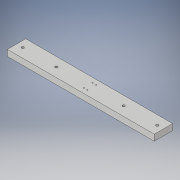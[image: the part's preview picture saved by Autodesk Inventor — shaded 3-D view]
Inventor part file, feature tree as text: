
AUTODESK INVENTOR PART (.ipt)
format: ipt  version: 2018 (Build 220112000, 112)  size: 114,688 bytes
history: native  units: in
note: dims shown in document units (in); Inventor stores cm internally (conversion verified against a paired STEP export)
features: sketch x3, hole x2, extrude x1
ambient origin geometry x8: Origin, YZ Plane, XZ Plane, XY Plane, X Axis, Y Axis, Z Axis, Center Point
bodies: Solid1 (feature_tree)
feature tree (6):
  extrude  "Extrusion1"  Depth=3.0in
  hole  "Hole1"  [1 undecoded]
  hole  "Hole2"  [1 undecoded]
  sketch  "Sketch1"  dims[d0=24.0in d1=3.0in]
  sketch  "Sketch2"  dims[d2=1.0in d3=0.0in d4=11.0in]
  sketch  "Sketch3"  dims[d5=5.5in d6=0.397in d7=0.75in d8=0.635in d9=0.25in d10=0.5635in d11=1.0in d12=0.8108in d13=0.575in d14=1.43in d15=0.156in d16=0.38in d17=0.385in d18=0.25in d19=0.5635in d20=0.536in d21=0.8108in]
note: 2 required parameter values undecoded (feature->parameter linkage not recoverable at this tier; creation-order binding heuristic only, values carry confidence <= 0.55)
